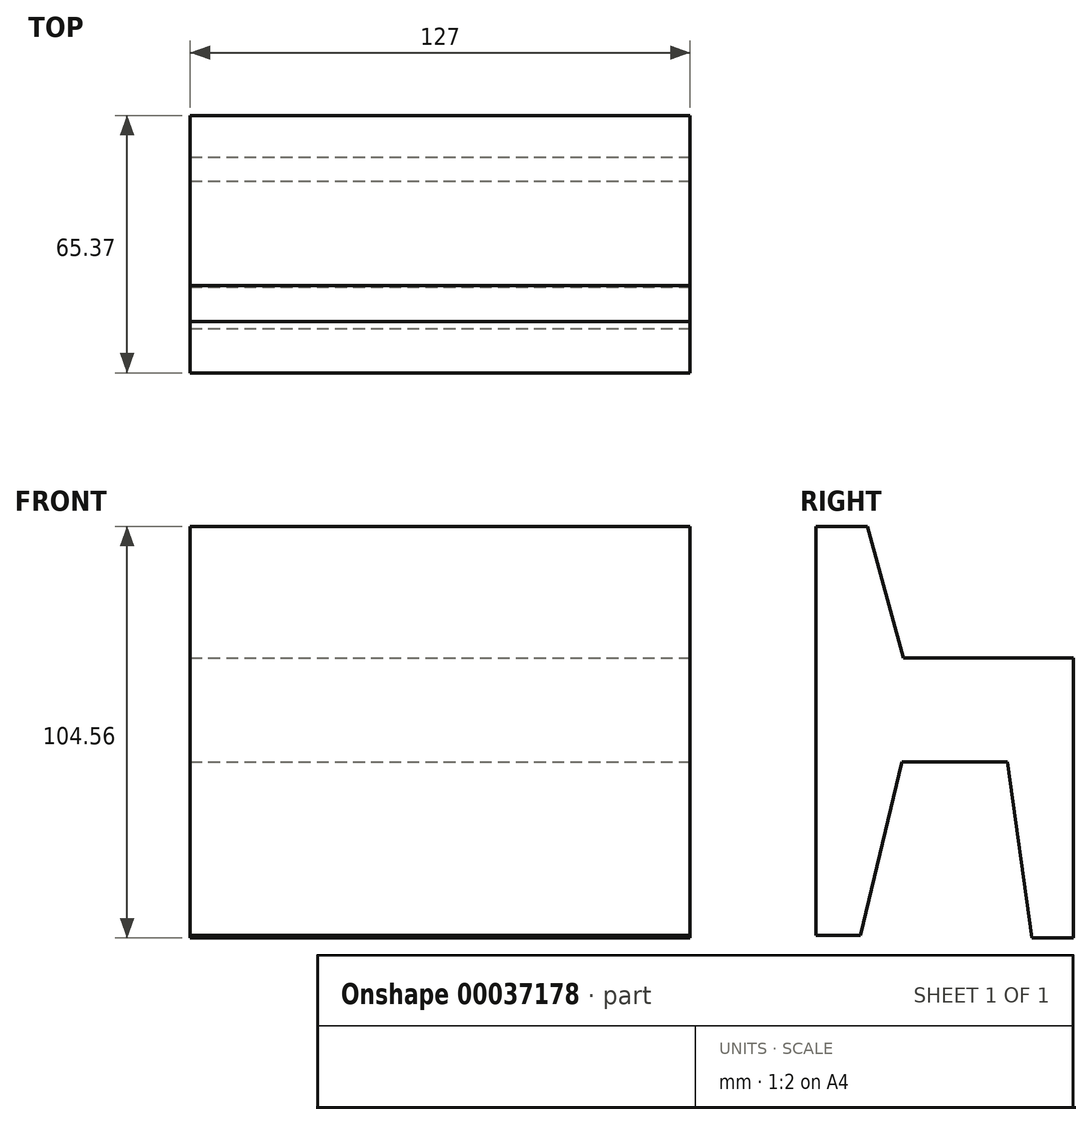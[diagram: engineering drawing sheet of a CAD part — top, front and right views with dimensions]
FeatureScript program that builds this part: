
annotation { "Feature Type Name" : "Feature", "Feature Type Description" : "" }
export const myFeature = defineFeature(function(context is Context, id is Id, definition is map)
    precondition{}
    {
        {
            var Q0;
            Q0=qCreatedBy(makeId("Right.planeOp"),FACE);
            var sketch = newSketch(context, id + "F0", { "sketchPlane" : qUnion([Q0])});
            skLineSegment(sketch, "E0", {"start": v(-65.37, 41.93) * mm, "end": v(-65.37, -47.7) * mm});
            skLineSegment(sketch, "E1", {"start": v(-65.37, -47.7) * mm, "end": v(-54.08, -47.7) * mm});
            skLineSegment(sketch, "E2", {"start": v(-54.08, -47.7) * mm, "end": v(-43.55, -3.7) * mm});
            skLineSegment(sketch, "E3", {"start": v(-43.55, -3.7) * mm, "end": v(-16.69, -3.7) * mm});
            skLineSegment(sketch, "E4", {"start": v(-16.69, -3.7) * mm, "end": v(-10.51, -48.35) * mm});
            skLineSegment(sketch, "E5", {"start": v(-10.51, -48.35) * mm, "end": v(0, -48.35) * mm});
            skLineSegment(sketch, "E6", {"start": v(0, -48.35) * mm, "end": v(0, 0) * mm});
            skLineSegment(sketch, "E7", {"start": v(0, 0) * mm, "end": v(0, 22.81) * mm});
            skLineSegment(sketch, "E8", {"start": v(0, 22.81) * mm, "end": v(-43.2, 22.81) * mm});
            skLineSegment(sketch, "E9", {"start": v(-43.2, 22.81) * mm, "end": v(-52.27, 56.21) * mm});
            skLineSegment(sketch, "E10", {"start": v(-52.27, 56.21) * mm, "end": v(-65.37, 56.21) * mm});
            skLineSegment(sketch, "E11", {"start": v(-65.37, 56.21) * mm, "end": v(-65.37, 41.93) * mm});
            skSolve(sketch);
        }
        {
            var Q0;
            Q0=sQuery(id+"F0.wireOp",EDGE,"E2");
            var Q1;
            Q1=sQuery(id+"F0.wireOp",EDGE,"E1");
            var Q2;
            Q2=sQuery(id+"F0.wireOp",EDGE,"E5");
            var Q3;
            Q3=sQuery(id+"F0.wireOp",EDGE,"E7");
            var Q4;
            Q4=sQuery(id+"F0.wireOp",EDGE,"E9");
            var Q5;
            Q5=sQuery(id+"F0.wireOp",EDGE,"E11");
            var Q6;
            Q6=sQuery(id+"F0.wireOp",EDGE,"E0");
            var Q7;
            Q7=sQuery(id+"F0.wireOp",EDGE,"E8");
            var Q8;
            Q8=sQuery(id+"F0.wireOp",EDGE,"E6");
            var Q9;
            Q9=sQuery(id+"F0.wireOp",EDGE,"E4");
            var Q10;
            Q10=sQuery(id+"F0.wireOp",EDGE,"E3");
            var Q11;
            Q11=sQuery(id+"F0.wireOp",EDGE,"E10");
            extrude(context, id + "F1", {"bodyType" : ToolBodyType.SURFACE, "surfaceEntities" : qUnion([Q0, Q1, Q2, Q3, Q4, Q5, Q6, Q7, Q8, Q9, Q10, Q11]), "depth" : 101.6 * mm, "hasSecondDirection" : true, "secondDirectionOppositeDirection" : true, "secondDirectionDepth" : 25.4 * mm});
        }
    });
